FCSTD DOCUMENT  (FreeCAD 0.19R)
Label: lens_set_up
License: All rights reserved
LicenseURL: http://en.wikipedia.org/wiki/All_rights_reserved
objects: Sketcher::SketchObject×1, PartDesign::Body×1, Spreadsheet::Sheet×1
note: 2 computed .brp shape members not serialized (recipe doc carries the construction recipe); baked Part::Feature solids carry a one-line shape summary decoded from their .brp

FEATURE [Sketcher::SketchObject] Sketch
  FullyConstrained = false
  MapMode = 5
  Support = -> [XY_Plane]
  expr: Constraints[24] = <<parameters>>.lens_length
  expr: Constraints[28] = <<parameters>>.centre_length
  expr: Constraints[21] = <<parameters>>.lens_length
  expr: Constraints[18] = <<parameters>>.lens_width / 2
  expr: Constraints[17] = <<parameters>>.lens_width
  expr: Constraints[10] = <<parameters>>.lens_length
  expr: Constraints[2] = <<parameters>>.stereo_angle
  expr: Constraints[13] = <<parameters>>.lens_width
  expr: Constraints[7] = <<parameters>>.lens_width / 2
  expr: Constraints[39] = 78 / 2
  expr: Constraints[6] = <<parameters>>.lens_width
  expr: Constraints[29] = <<parameters>>.centre_length
  expr: Constraints[3] = -<<parameters>>.stereo_angle / 2
  sketch-geometry (14):
    g0: LineSegment StartX=0 StartY=364.532 StartZ=0 EndX=-39.2295 EndY=-133.927 EndZ=0
    g1: LineSegment StartX=0 StartY=364.532 StartZ=0 EndX=39.2295 EndY=-133.927 EndZ=0
    g2: LineSegment StartX=-60.182 StartY=-94.261 StartZ=0 EndX=-12.3299 EndY=-98.027 EndZ=0
    g3: LineSegment StartX=-60.182 StartY=-94.261 StartZ=0 EndX=-52.9559 EndY=-2.44489 EndZ=0
    g4: LineSegment StartX=-52.9559 StartY=-2.44489 StartZ=0 EndX=-5.10385 EndY=-6.21093 EndZ=0
    g5: LineSegment StartX=-12.3299 StartY=-98.027 StartZ=0 EndX=-5.10385 EndY=-6.21093 EndZ=0
    g6: LineSegment StartX=12.3299 StartY=-98.027 StartZ=0 EndX=60.182 EndY=-94.261 EndZ=0
    g7: LineSegment StartX=12.3299 StartY=-98.027 StartZ=0 EndX=5.10385 EndY=-6.21093 EndZ=0
    g8: LineSegment StartX=60.182 StartY=-94.261 StartZ=0 EndX=52.9559 EndY=-2.44489 EndZ=0
    g9: LineSegment StartX=5.10385 StartY=-6.21093 StartZ=0 EndX=52.9559 EndY=-2.44489 EndZ=0
    g10: LineSegment StartX=-39 StartY=282.688 StartZ=0 EndX=39 EndY=282.688 EndZ=0
    g11: LineSegment StartX=39 StartY=282.688 StartZ=0 EndX=39 EndY=75.9808 EndZ=0
    g12: LineSegment StartX=39 StartY=75.9808 StartZ=0 EndX=-39 EndY=75.9808 EndZ=0
    g13: LineSegment StartX=-39 StartY=75.9808 StartZ=0 EndX=-39 EndY=282.688 EndZ=0
  constraints (40):
    c: PointOnObject(g0,g-2)
    c: Coincident(g1,g0)
    c: Angle(g0,g1) = 0.15708
    c: Angle(g1,g-2) = -0.0785398
    c: Distance(g0) = 500
    c: Distance(g1) = 500
    c: Distance(g2) = 48
    c: Distance(g2,g0) = 24
    c: Perpendicular(g0,g2)
    c: Coincident(g3,g2)
    c: Distance(g3) = 92.1
    c: Parallel(g0,g3)
    c: Coincident(g4,g3)
    c: Distance(g4) = 48
    c: Perpendicular(g3,g4)
    c: Coincident(g5,g2)
    c: Coincident(g5,g4)
    c: Distance(g6) = 48
    c: Distance(g6,g1) = 24
    c: Perpendicular(g1,g6)
    c: Coincident(g7,g6)
    c: Distance(g7) = 92.1
    c: Perpendicular(g7,g6)
    c: Coincident(g8,g6)
    c: Distance(g8) = 92.1
    c: Coincident(g9,g7)
    c: Coincident(g9,g8)
    c: Perpendicular(g6,g8)
    c: Distance(g0,g9) = 370
    c: Distance(g0,g4) = 370
    c: Coincident(g10,g11)
    c: Coincident(g11,g12)
    c: Coincident(g12,g13)
    c: Coincident(g13,g10)
    c: Horizontal(g10)
    c: Horizontal(g12)
    c: Vertical(g11)
    c: Vertical(g13)
    c: DistanceX(g12,g12) = 78
    c: DistanceX(g-1,g11) = 39
FEATURE [PartDesign::Body] Body
  Group = -> [Sketch]
  Origin = -> Origin
FEATURE [Spreadsheet::Sheet] Spreadsheet  label="parameters"
  cells = A2=Stereo angle; B2(stereo_angle)=9; A3=lens length; B3(lens_length)=92.09999999999999; A4=lens width; B4(lens_width)=48; A5=length to centre; B5(centre_length)=370
